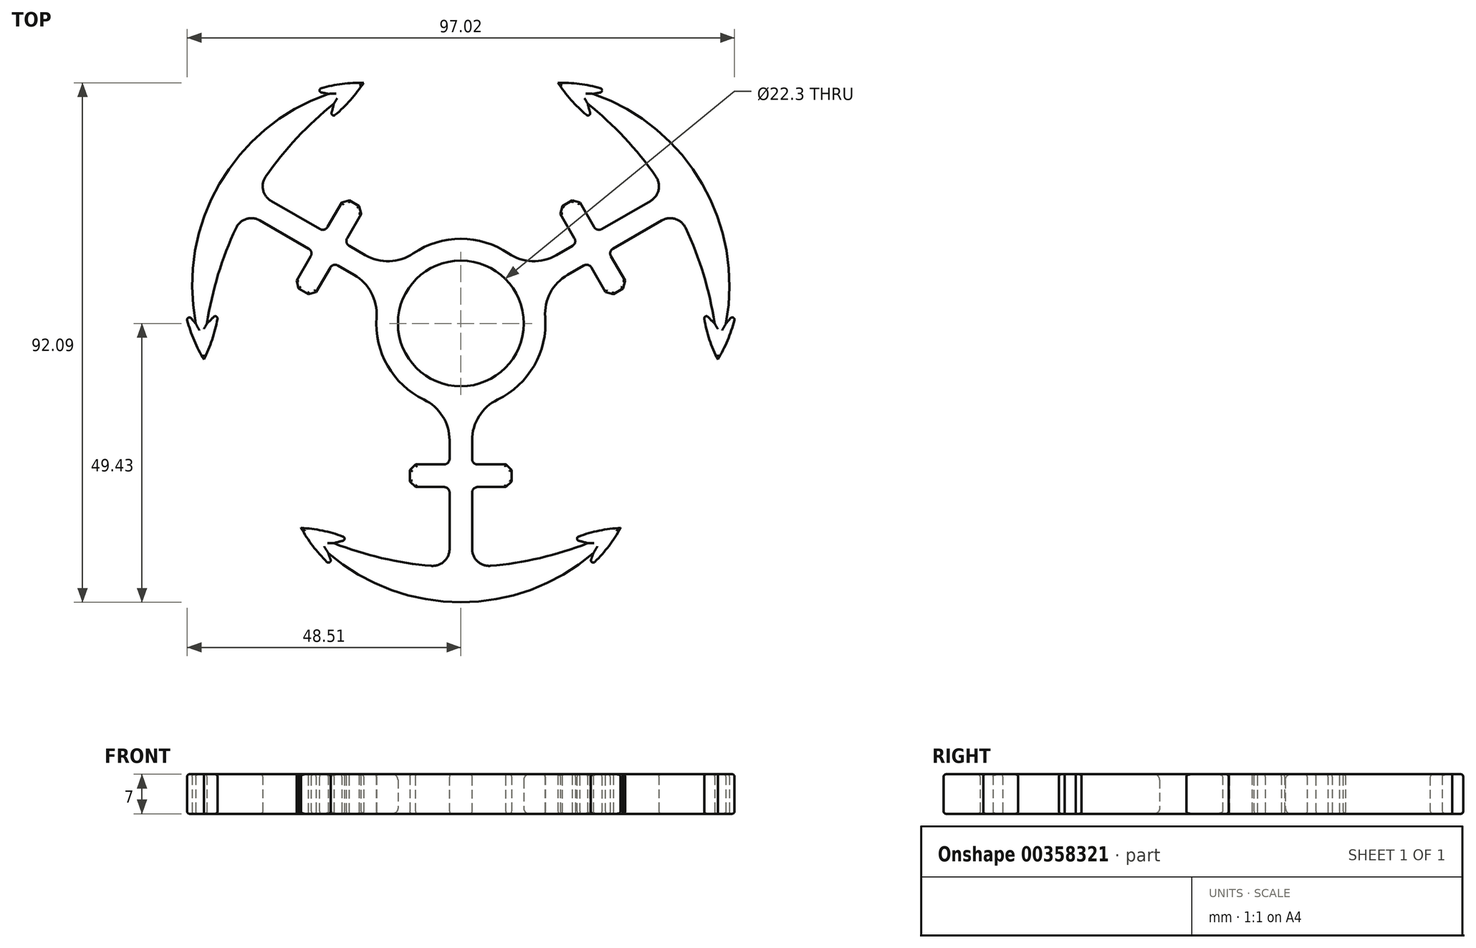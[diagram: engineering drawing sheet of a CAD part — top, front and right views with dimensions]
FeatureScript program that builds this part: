
annotation { "Feature Type Name" : "Feature", "Feature Type Description" : "" }
export const myFeature = defineFeature(function(context is Context, id is Id, definition is map)
    precondition{}
    {
        {
            var Q0;
            Q0=qCreatedBy(makeId("Top.planeOp"),FACE);
            var sketch = newSketch(context, id + "F0", { "sketchPlane" : qUnion([Q0])});
            skCircle(sketch, "E0", {"center": v(0, 0) * mm, "radius": 11.15 * mm});
            skArc(sketch, "E1", {"start": v(-13.87, 5.7) * mm, "mid": v(-13, -7.5) * mm, "end": v(-2, -14.87) * mm});
            skCircle(sketch, "E2", {"center": v(0, 0) * mm, "radius": 45 * mm, "construction": true});
            skLineSegment(sketch, "E3", {"start": v(0, 0) * mm, "end": v(0, -53.16) * mm, "construction": true});
            skLineSegment(sketch, "E4", {"start": v(0, 0) * mm, "end": v(-28.72, -49.74) * mm, "construction": true});
            skLineSegment(sketch, "E5", {"start": v(0, 0) * mm, "end": v(28.85, -49.97) * mm, "construction": true});
            skCircle(sketch, "E6.0", {"center": v(0, 0) * mm, "radius": 47 * mm, "construction": true});
            skArc(sketch, "E7", {"start": v(-22.5, -38.97) * mm, "mid": v(-12.43, -41.94) * mm, "end": v(-2, -43.17) * mm});
            skArc(sketch, "E8", {"start": v(-23.5, -40.7) * mm, "mid": v(0, -49.43) * mm, "end": v(23.5, -40.7) * mm});
            skLineSegment(sketch, "E9", {"start": v(0, 0) * mm, "end": v(-34.06, -43.6) * mm, "construction": true});
            skLineSegment(sketch, "E10", {"start": v(0, 0) * mm, "end": v(33.07, -42.33) * mm, "construction": true});
            skCircle(sketch, "E11.0", {"center": v(0, 0) * mm, "radius": 46 * mm, "construction": true});
            skCircle(sketch, "E12.0", {"center": v(0, 0) * mm, "radius": 43 * mm, "construction": true});
            skCircle(sketch, "E13.0", {"center": v(0, 0) * mm, "radius": 49 * mm, "construction": true});
            skLineSegment(sketch, "E14", {"start": v(0, 0) * mm, "end": v(-25.8, -50.64) * mm, "construction": true});
            skLineSegment(sketch, "E15", {"start": v(0, 0) * mm, "end": v(25.98, -51) * mm, "construction": true});
            skArc(sketch, "E16", {"start": v(-19.52, -38.31) * mm, "mid": v(-23.83, -36.9) * mm, "end": v(-28.32, -36.25) * mm});
            skArc(sketch, "E17", {"start": v(-28.32, -36.25) * mm, "mid": v(-25.63, -40.24) * mm, "end": v(-22.25, -43.66) * mm});
            skArc(sketch, "E18", {"start": v(-23.5, -40.7) * mm, "mid": v(-22.95, -42.21) * mm, "end": v(-22.25, -43.66) * mm});
            skArc(sketch, "E19", {"start": v(-19.52, -38.31) * mm, "mid": v(-21.03, -38.57) * mm, "end": v(-22.5, -38.97) * mm});
            skArc(sketch, "E20", {"start": v(28.32, -36.25) * mm, "mid": v(23.83, -36.9) * mm, "end": v(19.52, -38.31) * mm});
            skArc(sketch, "E21", {"start": v(22.25, -43.66) * mm, "mid": v(25.63, -40.24) * mm, "end": v(28.32, -36.25) * mm});
            skArc(sketch, "E22", {"start": v(22.25, -43.66) * mm, "mid": v(22.95, -42.21) * mm, "end": v(23.5, -40.7) * mm});
            skArc(sketch, "E23", {"start": v(22.5, -38.97) * mm, "mid": v(21.03, -38.57) * mm, "end": v(19.52, -38.31) * mm});
            skArc(sketch, "E24.trimOffspring", {"start": v(2, -43.17) * mm, "mid": v(12.43, -41.94) * mm, "end": v(22.5, -38.97) * mm});
            skLineSegment(sketch, "E25.trimOffspring", {"start": v(-2, -14.87) * mm, "end": v(-2, -43.17) * mm});
            skLineSegment(sketch, "E26.trimOffspring", {"start": v(2, -14.87) * mm, "end": v(2, -43.17) * mm});
            skArc(sketch, "E27.1.0", {"start": v(42.94, 2.25) * mm, "mid": v(43.91, 1.07) * mm, "end": v(45, 0) * mm});
            skArc(sketch, "E27.1.1", {"start": v(45.55, -6.4) * mm, "mid": v(47.66, -2.08) * mm, "end": v(48.93, 2.56) * mm});
            skArc(sketch, "E27.1.2", {"start": v(22.5, 38.97) * mm, "mid": v(22.89, 37.5) * mm, "end": v(23.42, 36.06) * mm});
            skArc(sketch, "E27.1.3", {"start": v(42.94, 2.25) * mm, "mid": v(43.87, -2.2) * mm, "end": v(45.55, -6.4) * mm});
            skArc(sketch, "E27.1.4", {"start": v(17.23, 42.65) * mm, "mid": v(20.04, 39.09) * mm, "end": v(23.42, 36.06) * mm});
            skArc(sketch, "E27.1.5", {"start": v(26.69, 41.1) * mm, "mid": v(22.03, 42.31) * mm, "end": v(17.23, 42.65) * mm});
            skArc(sketch, "E27.1.6", {"start": v(36.38, 23.31) * mm, "mid": v(30.1, 31.73) * mm, "end": v(22.5, 38.97) * mm});
            skArc(sketch, "E27.1.7", {"start": v(47, 0) * mm, "mid": v(42.8, 24.72) * mm, "end": v(23.5, 40.7) * mm});
            skArc(sketch, "E27.1.8", {"start": v(45, 0) * mm, "mid": v(42.53, 10.2) * mm, "end": v(38.38, 19.85) * mm});
            skArc(sketch, "E27.1.9", {"start": v(47, 0) * mm, "mid": v(48.04, 1.23) * mm, "end": v(48.93, 2.56) * mm});
            skArc(sketch, "E27.1.10", {"start": v(26.69, 41.1) * mm, "mid": v(25.08, 40.98) * mm, "end": v(23.5, 40.7) * mm});
            skLineSegment(sketch, "E27.1.11", {"start": v(13.87, 5.7) * mm, "end": v(38.38, 19.85) * mm});
            skLineSegment(sketch, "E27.1.12", {"start": v(11.87, 9.17) * mm, "end": v(36.38, 23.31) * mm});
            skArc(sketch, "E27.2.0", {"start": v(-23.42, 36.06) * mm, "mid": v(-22.89, 37.5) * mm, "end": v(-22.5, 38.97) * mm});
            skArc(sketch, "E27.2.1", {"start": v(-17.23, 42.65) * mm, "mid": v(-22.03, 42.31) * mm, "end": v(-26.69, 41.1) * mm});
            skArc(sketch, "E27.2.2", {"start": v(-45, 0) * mm, "mid": v(-43.91, 1.07) * mm, "end": v(-42.94, 2.25) * mm});
            skArc(sketch, "E27.2.3", {"start": v(-23.42, 36.06) * mm, "mid": v(-20.04, 39.09) * mm, "end": v(-17.23, 42.65) * mm});
            skArc(sketch, "E27.2.4", {"start": v(-45.55, -6.4) * mm, "mid": v(-43.87, -2.2) * mm, "end": v(-42.94, 2.25) * mm});
            skArc(sketch, "E27.2.5", {"start": v(-48.93, 2.56) * mm, "mid": v(-47.66, -2.08) * mm, "end": v(-45.55, -6.4) * mm});
            skArc(sketch, "E27.2.6", {"start": v(-38.38, 19.85) * mm, "mid": v(-42.53, 10.2) * mm, "end": v(-45, 0) * mm});
            skArc(sketch, "E27.2.7", {"start": v(-23.5, 40.7) * mm, "mid": v(-42.8, 24.72) * mm, "end": v(-47, 0) * mm});
            skArc(sketch, "E27.2.8", {"start": v(-22.5, 38.97) * mm, "mid": v(-30.1, 31.73) * mm, "end": v(-36.38, 23.31) * mm});
            skArc(sketch, "E27.2.9", {"start": v(-23.5, 40.7) * mm, "mid": v(-25.08, 40.98) * mm, "end": v(-26.69, 41.1) * mm});
            skArc(sketch, "E27.2.10", {"start": v(-48.93, 2.56) * mm, "mid": v(-48.04, 1.23) * mm, "end": v(-47, 0) * mm});
            skLineSegment(sketch, "E27.2.11", {"start": v(-11.87, 9.17) * mm, "end": v(-36.38, 23.31) * mm});
            skLineSegment(sketch, "E27.2.12", {"start": v(-13.87, 5.7) * mm, "end": v(-38.38, 19.85) * mm});
            skArc(sketch, "E28.trimOffspring", {"start": v(11.87, 9.17) * mm, "mid": v(0, 15) * mm, "end": v(-11.87, 9.17) * mm});
            skArc(sketch, "E29.trimOffspring", {"start": v(2, -14.87) * mm, "mid": v(13, -7.5) * mm, "end": v(13.87, 5.7) * mm});
            skSolve(sketch);
        }
        {
            var Q0;
            Q0 = qSketchRegion(id + "F0", true);
            extrude(context, id + "F1", {"entities" : qUnion([Q0]), "depth" : 7 * mm});
        }
        {
            var Q0;
            Q0=makeQuery(id+"F1.opExtrude","SWEPT_EDGE",EDGE,{"disambiguationData":[OSD([sQuery(id+"F0.wireOp",EDGE,"E26.trimOffspring"),sQuery(id+"F0.wireOp",EDGE,"E29.trimOffspring")])]});
            var Q1;
            Q1=makeQuery(id+"F1.opExtrude","SWEPT_EDGE",EDGE,{"disambiguationData":[OSD([sQuery(id+"F0.wireOp",EDGE,"E27.2.11"),sQuery(id+"F0.wireOp",EDGE,"E28.trimOffspring")])]});
            var Q2;
            Q2=makeQuery(id+"F1.opExtrude","SWEPT_EDGE",EDGE,{"disambiguationData":[OSD([sQuery(id+"F0.wireOp",EDGE,"E27.1.12"),sQuery(id+"F0.wireOp",EDGE,"E28.trimOffspring")])]});
            var Q3;
            Q3=makeQuery(id+"F1.opExtrude","SWEPT_EDGE",EDGE,{"disambiguationData":[OSD([sQuery(id+"F0.wireOp",EDGE,"E27.1.11"),sQuery(id+"F0.wireOp",EDGE,"E29.trimOffspring")])]});
            var Q4;
            Q4=makeQuery(id+"F1.opExtrude","SWEPT_EDGE",EDGE,{"disambiguationData":[OSD([sQuery(id+"F0.wireOp",EDGE,"E1"),sQuery(id+"F0.wireOp",EDGE,"E27.2.12")])]});
            var Q5;
            Q5=makeQuery(id+"F1.opExtrude","SWEPT_EDGE",EDGE,{"disambiguationData":[OSD([sQuery(id+"F0.wireOp",EDGE,"E1"),sQuery(id+"F0.wireOp",EDGE,"E25.trimOffspring")])]});
            fillet(context, id + "F2", {"entities" : qUnion([Q0, Q1, Q2, Q3, Q4, Q5]), "radius" : 8 * mm, "tangentPropagation" : true, "allowEdgeOverflow" : false});
        }
        {
            var Q0;
            Q0=makeQuery(id+"F1.opExtrude","SWEPT_EDGE",EDGE,{"disambiguationData":[OSD([sQuery(id+"F0.wireOp",EDGE,"E27.1.6"),sQuery(id+"F0.wireOp",EDGE,"E27.1.12")])]});
            var Q1;
            Q1=makeQuery(id+"F1.opExtrude","SWEPT_EDGE",EDGE,{"disambiguationData":[OSD([sQuery(id+"F0.wireOp",EDGE,"E7"),sQuery(id+"F0.wireOp",EDGE,"E25.trimOffspring")])]});
            var Q2;
            Q2=makeQuery(id+"F1.opExtrude","SWEPT_EDGE",EDGE,{"disambiguationData":[OSD([sQuery(id+"F0.wireOp",EDGE,"E27.2.8"),sQuery(id+"F0.wireOp",EDGE,"E27.2.11")])]});
            var Q3;
            Q3=makeQuery(id+"F1.opExtrude","SWEPT_EDGE",EDGE,{"disambiguationData":[OSD([sQuery(id+"F0.wireOp",EDGE,"E27.2.6"),sQuery(id+"F0.wireOp",EDGE,"E27.2.12")])]});
            var Q4;
            Q4=makeQuery(id+"F1.opExtrude","SWEPT_EDGE",EDGE,{"disambiguationData":[OSD([sQuery(id+"F0.wireOp",EDGE,"E27.1.8"),sQuery(id+"F0.wireOp",EDGE,"E27.1.11")])]});
            var Q5;
            Q5=makeQuery(id+"F1.opExtrude","SWEPT_EDGE",EDGE,{"disambiguationData":[OSD([sQuery(id+"F0.wireOp",EDGE,"E24.trimOffspring"),sQuery(id+"F0.wireOp",EDGE,"E26.trimOffspring")])]});
            fillet(context, id + "F3", {"entities" : qUnion([Q0, Q1, Q2, Q3, Q4, Q5]), "radius" : 3 * mm, "tangentPropagation" : true, "allowEdgeOverflow" : false});
        }
        {
            var Q0;
            Q0=makeQuery(id+"F1.opExtrude","SWEPT_EDGE",EDGE,{"disambiguationData":[OSD([sQuery(id+"F0.wireOp",EDGE,"E27.2.0"),sQuery(id+"F0.wireOp",EDGE,"E27.2.3")])]});
            var Q1;
            Q1=makeQuery(id+"F1.opExtrude","SWEPT_EDGE",EDGE,{"disambiguationData":[OSD([sQuery(id+"F0.wireOp",EDGE,"E27.2.1"),sQuery(id+"F0.wireOp",EDGE,"E27.2.9")])]});
            var Q2;
            Q2=makeQuery(id+"F1.opExtrude","SWEPT_EDGE",EDGE,{"disambiguationData":[OSD([sQuery(id+"F0.wireOp",EDGE,"E27.2.5"),sQuery(id+"F0.wireOp",EDGE,"E27.2.10")])]});
            var Q3;
            Q3=makeQuery(id+"F1.opExtrude","SWEPT_EDGE",EDGE,{"disambiguationData":[OSD([sQuery(id+"F0.wireOp",EDGE,"E27.2.2"),sQuery(id+"F0.wireOp",EDGE,"E27.2.4")])]});
            var Q4;
            Q4=makeQuery(id+"F1.opExtrude","SWEPT_EDGE",EDGE,{"disambiguationData":[OSD([sQuery(id+"F0.wireOp",EDGE,"E27.1.2"),sQuery(id+"F0.wireOp",EDGE,"E27.1.4")])]});
            var Q5;
            Q5=makeQuery(id+"F1.opExtrude","SWEPT_EDGE",EDGE,{"disambiguationData":[OSD([sQuery(id+"F0.wireOp",EDGE,"E27.1.0"),sQuery(id+"F0.wireOp",EDGE,"E27.1.3")])]});
            var Q6;
            Q6=makeQuery(id+"F1.opExtrude","SWEPT_EDGE",EDGE,{"disambiguationData":[OSD([sQuery(id+"F0.wireOp",EDGE,"E17"),sQuery(id+"F0.wireOp",EDGE,"E18")])]});
            var Q7;
            Q7=makeQuery(id+"F1.opExtrude","SWEPT_EDGE",EDGE,{"disambiguationData":[OSD([sQuery(id+"F0.wireOp",EDGE,"E21"),sQuery(id+"F0.wireOp",EDGE,"E22")])]});
            var Q8;
            Q8=makeQuery(id+"F1.opExtrude","SWEPT_EDGE",EDGE,{"disambiguationData":[OSD([sQuery(id+"F0.wireOp",EDGE,"E20"),sQuery(id+"F0.wireOp",EDGE,"E23")])]});
            var Q9;
            Q9=makeQuery(id+"F1.opExtrude","SWEPT_EDGE",EDGE,{"disambiguationData":[OSD([sQuery(id+"F0.wireOp",EDGE,"E16"),sQuery(id+"F0.wireOp",EDGE,"E19")])]});
            var Q10;
            Q10=makeQuery(id+"F1.opExtrude","SWEPT_EDGE",EDGE,{"disambiguationData":[OSD([sQuery(id+"F0.wireOp",EDGE,"E27.1.5"),sQuery(id+"F0.wireOp",EDGE,"E27.1.10")])]});
            var Q11;
            Q11=makeQuery(id+"F1.opExtrude","SWEPT_EDGE",EDGE,{"disambiguationData":[OSD([sQuery(id+"F0.wireOp",EDGE,"E27.1.1"),sQuery(id+"F0.wireOp",EDGE,"E27.1.9")])]});
            fillet(context, id + "F4", {"entities" : qUnion([Q0, Q1, Q2, Q3, Q4, Q5, Q6, Q7, Q8, Q9, Q10, Q11]), "radius" : .4 * mm, "allowEdgeOverflow" : false});
        }
        {
            var Q0;
            Q0=qCreatedBy(makeId("Top.planeOp"),FACE);
            var sketch = newSketch(context, id + "F5", { "sketchPlane" : qUnion([Q0])});
            skLineSegment(sketch, "E30.bottom", {"start": v(-9, -25) * mm, "end": v(9, -25) * mm});
            skLineSegment(sketch, "E30.top", {"start": v(-9, -29) * mm, "end": v(9, -29) * mm});
            skLineSegment(sketch, "E30.left", {"start": v(-9, -25) * mm, "end": v(-9, -29) * mm});
            skLineSegment(sketch, "E30.right", {"start": v(9, -25) * mm, "end": v(9, -29) * mm});
            skLineSegment(sketch, "E31.1.0", {"start": v(26.15, 4.7) * mm, "end": v(17.15, 20.3) * mm});
            skLineSegment(sketch, "E31.1.1", {"start": v(29.61, 6.7) * mm, "end": v(20.61, 22.3) * mm});
            skLineSegment(sketch, "E31.1.2", {"start": v(26.15, 4.7) * mm, "end": v(29.61, 6.7) * mm});
            skLineSegment(sketch, "E31.1.3", {"start": v(17.15, 20.3) * mm, "end": v(20.61, 22.3) * mm});
            skLineSegment(sketch, "E31.2.0", {"start": v(-17.15, 20.3) * mm, "end": v(-26.15, 4.7) * mm});
            skLineSegment(sketch, "E31.2.1", {"start": v(-20.61, 22.3) * mm, "end": v(-29.61, 6.7) * mm});
            skLineSegment(sketch, "E31.2.2", {"start": v(-17.15, 20.3) * mm, "end": v(-20.61, 22.3) * mm});
            skLineSegment(sketch, "E31.2.3", {"start": v(-26.15, 4.7) * mm, "end": v(-29.61, 6.7) * mm});
            skPoint(sketch, "E31.center", {"position": v(0, 0) * mm});
            skSolve(sketch);
        }
        {
            var Q0;
            Q0 = qSketchRegion(id + "F5", true);
            extrude(context, id + "F6", {"entities" : qUnion([Q0]), "operationType" : NewBodyOperationType.ADD, "depth" : 7 * mm});
        }
        {
            var Q0;
            Q0=makeQuery(id+"F6.opExtrude","SWEPT_EDGE",EDGE,{"disambiguationData":[OSD([sQuery(id+"F5.wireOp",EDGE,"E31.2.0"),sQuery(id+"F5.wireOp",EDGE,"E31.2.3")])]});
            var Q1;
            Q1=makeQuery(id+"F6.opExtrude","SWEPT_EDGE",EDGE,{"disambiguationData":[OSD([sQuery(id+"F5.wireOp",EDGE,"E31.2.1"),sQuery(id+"F5.wireOp",EDGE,"E31.2.3")])]});
            var Q2;
            Q2=makeQuery(id+"F6.opExtrude","SWEPT_EDGE",EDGE,{"disambiguationData":[OSD([sQuery(id+"F5.wireOp",EDGE,"E31.2.0"),sQuery(id+"F5.wireOp",EDGE,"E31.2.2")])]});
            var Q3;
            Q3=makeQuery(id+"F6.opExtrude","SWEPT_EDGE",EDGE,{"disambiguationData":[OSD([sQuery(id+"F5.wireOp",EDGE,"E30.top"),sQuery(id+"F5.wireOp",EDGE,"E30.left")])]});
            var Q4;
            Q4=makeQuery(id+"F6.opExtrude","SWEPT_EDGE",EDGE,{"disambiguationData":[OSD([sQuery(id+"F5.wireOp",EDGE,"E30.top"),sQuery(id+"F5.wireOp",EDGE,"E30.right")])]});
            var Q5;
            Q5=makeQuery(id+"F6.opExtrude","SWEPT_EDGE",EDGE,{"disambiguationData":[OSD([sQuery(id+"F5.wireOp",EDGE,"E31.1.0"),sQuery(id+"F5.wireOp",EDGE,"E31.1.2")])]});
            var Q6;
            Q6=makeQuery(id+"F6.opExtrude","SWEPT_EDGE",EDGE,{"disambiguationData":[OSD([sQuery(id+"F5.wireOp",EDGE,"E31.1.1"),sQuery(id+"F5.wireOp",EDGE,"E31.1.2")])]});
            var Q7;
            Q7=makeQuery(id+"F6.opExtrude","SWEPT_EDGE",EDGE,{"disambiguationData":[OSD([sQuery(id+"F5.wireOp",EDGE,"E31.1.0"),sQuery(id+"F5.wireOp",EDGE,"E31.1.3")])]});
            var Q8;
            Q8=makeQuery(id+"F6.opExtrude","SWEPT_EDGE",EDGE,{"disambiguationData":[OSD([sQuery(id+"F5.wireOp",EDGE,"E30.bottom"),sQuery(id+"F5.wireOp",EDGE,"E30.right")])]});
            var Q9;
            Q9=makeQuery(id+"F6.opExtrude","SWEPT_EDGE",EDGE,{"disambiguationData":[OSD([sQuery(id+"F5.wireOp",EDGE,"E30.bottom"),sQuery(id+"F5.wireOp",EDGE,"E30.left")])]});
            var Q10;
            Q10=makeQuery(id+"F6.opExtrude","SWEPT_EDGE",EDGE,{"disambiguationData":[OSD([sQuery(id+"F5.wireOp",EDGE,"E31.1.1"),sQuery(id+"F5.wireOp",EDGE,"E31.1.3")])]});
            var Q11;
            Q11=makeQuery(id+"F6.opExtrude","SWEPT_EDGE",EDGE,{"disambiguationData":[OSD([sQuery(id+"F5.wireOp",EDGE,"E31.2.1"),sQuery(id+"F5.wireOp",EDGE,"E31.2.2")])]});
            chamfer(context, id + "F7", {"entities" : qUnion([Q0, Q1, Q2, Q3, Q4, Q5, Q6, Q7, Q8, Q9, Q10, Q11]), "width" : 1 * mm, "tangentPropagation" : true});
        }
        {
            var Q0;
            Q0=makeQuery(id+"F1.opExtrude","SWEPT_FACE",FACE,{"disambiguationData":[OSD([sQuery(id+"F0.wireOp",EDGE,"E0")])]});
            fillet(context, id + "F8", {"entities" : qUnion([Q0]), "radius" : 1 * mm, "tangentPropagation" : true, "allowEdgeOverflow" : false});
        }
        {
            var Q0;
            Q0=makeQuery(id+"F6.boolean.opBoolean","INTERSECT",EDGE,{"derivedFrom":[makeQuery(id+"F1.opExtrude","SWEPT_FACE",FACE,{"disambiguationData":[OSD([sQuery(id+"F0.wireOp",EDGE,"E26.trimOffspring")])]}),makeQuery(id+"F6.opExtrude","SWEPT_FACE",FACE,{"disambiguationData":[OSD([sQuery(id+"F5.wireOp",EDGE,"E30.top")])]})]});
            var Q1;
            Q1=makeQuery(id+"F6.boolean.opBoolean","INTERSECT",EDGE,{"derivedFrom":[makeQuery(id+"F1.opExtrude","SWEPT_FACE",FACE,{"disambiguationData":[OSD([sQuery(id+"F0.wireOp",EDGE,"E27.1.11")])]}),makeQuery(id+"F6.opExtrude","SWEPT_FACE",FACE,{"disambiguationData":[OSD([sQuery(id+"F5.wireOp",EDGE,"E31.1.1")])]})]});
            var Q2;
            Q2=makeQuery(id+"F6.boolean.opBoolean","INTERSECT",EDGE,{"derivedFrom":[makeQuery(id+"F1.opExtrude","SWEPT_FACE",FACE,{"disambiguationData":[OSD([sQuery(id+"F0.wireOp",EDGE,"E27.2.12")])]}),makeQuery(id+"F6.opExtrude","SWEPT_FACE",FACE,{"disambiguationData":[OSD([sQuery(id+"F5.wireOp",EDGE,"E31.2.1")])]})]});
            var Q3;
            Q3=makeQuery(id+"F6.boolean.opBoolean","INTERSECT",EDGE,{"derivedFrom":[makeQuery(id+"F1.opExtrude","SWEPT_FACE",FACE,{"disambiguationData":[OSD([sQuery(id+"F0.wireOp",EDGE,"E25.trimOffspring")])]}),makeQuery(id+"F6.opExtrude","SWEPT_FACE",FACE,{"disambiguationData":[OSD([sQuery(id+"F5.wireOp",EDGE,"E30.top")])]})]});
            var Q4;
            Q4=makeQuery(id+"F6.boolean.opBoolean","INTERSECT",EDGE,{"derivedFrom":[makeQuery(id+"F1.opExtrude","SWEPT_FACE",FACE,{"disambiguationData":[OSD([sQuery(id+"F0.wireOp",EDGE,"E27.1.11")])]}),makeQuery(id+"F6.opExtrude","SWEPT_FACE",FACE,{"disambiguationData":[OSD([sQuery(id+"F5.wireOp",EDGE,"E31.1.0")])]})]});
            var Q5;
            Q5=makeQuery(id+"F6.boolean.opBoolean","INTERSECT",EDGE,{"derivedFrom":[makeQuery(id+"F1.opExtrude","SWEPT_FACE",FACE,{"disambiguationData":[OSD([sQuery(id+"F0.wireOp",EDGE,"E27.2.12")])]}),makeQuery(id+"F6.opExtrude","SWEPT_FACE",FACE,{"disambiguationData":[OSD([sQuery(id+"F5.wireOp",EDGE,"E31.2.0")])]})]});
            var Q6;
            Q6=makeQuery(id+"F6.boolean.opBoolean","INTERSECT",EDGE,{"derivedFrom":[makeQuery(id+"F1.opExtrude","SWEPT_FACE",FACE,{"disambiguationData":[OSD([sQuery(id+"F0.wireOp",EDGE,"E25.trimOffspring")])]}),makeQuery(id+"F6.opExtrude","SWEPT_FACE",FACE,{"disambiguationData":[OSD([sQuery(id+"F5.wireOp",EDGE,"E30.bottom")])]})]});
            var Q7;
            Q7=makeQuery(id+"F6.boolean.opBoolean","INTERSECT",EDGE,{"derivedFrom":[makeQuery(id+"F1.opExtrude","SWEPT_FACE",FACE,{"disambiguationData":[OSD([sQuery(id+"F0.wireOp",EDGE,"E27.1.12")])]}),makeQuery(id+"F6.opExtrude","SWEPT_FACE",FACE,{"disambiguationData":[OSD([sQuery(id+"F5.wireOp",EDGE,"E31.1.0")])]})]});
            var Q8;
            Q8=makeQuery(id+"F6.boolean.opBoolean","INTERSECT",EDGE,{"derivedFrom":[makeQuery(id+"F1.opExtrude","SWEPT_FACE",FACE,{"disambiguationData":[OSD([sQuery(id+"F0.wireOp",EDGE,"E27.2.11")])]}),makeQuery(id+"F6.opExtrude","SWEPT_FACE",FACE,{"disambiguationData":[OSD([sQuery(id+"F5.wireOp",EDGE,"E31.2.1")])]})]});
            var Q9;
            Q9=makeQuery(id+"F6.boolean.opBoolean","INTERSECT",EDGE,{"derivedFrom":[makeQuery(id+"F1.opExtrude","SWEPT_FACE",FACE,{"disambiguationData":[OSD([sQuery(id+"F0.wireOp",EDGE,"E27.1.12")])]}),makeQuery(id+"F6.opExtrude","SWEPT_FACE",FACE,{"disambiguationData":[OSD([sQuery(id+"F5.wireOp",EDGE,"E31.1.1")])]})]});
            var Q10;
            Q10=makeQuery(id+"F6.boolean.opBoolean","INTERSECT",EDGE,{"derivedFrom":[makeQuery(id+"F1.opExtrude","SWEPT_FACE",FACE,{"disambiguationData":[OSD([sQuery(id+"F0.wireOp",EDGE,"E26.trimOffspring")])]}),makeQuery(id+"F6.opExtrude","SWEPT_FACE",FACE,{"disambiguationData":[OSD([sQuery(id+"F5.wireOp",EDGE,"E30.bottom")])]})]});
            var Q11;
            Q11=makeQuery(id+"F6.boolean.opBoolean","INTERSECT",EDGE,{"derivedFrom":[makeQuery(id+"F1.opExtrude","SWEPT_FACE",FACE,{"disambiguationData":[OSD([sQuery(id+"F0.wireOp",EDGE,"E27.2.11")])]}),makeQuery(id+"F6.opExtrude","SWEPT_FACE",FACE,{"disambiguationData":[OSD([sQuery(id+"F5.wireOp",EDGE,"E31.2.0")])]})]});
            fillet(context, id + "F9", {"entities" : qUnion([Q0, Q1, Q2, Q3, Q4, Q5, Q6, Q7, Q8, Q9, Q10, Q11]), "radius" : 1 * mm, "tangentPropagation" : true, "allowEdgeOverflow" : false});
        }
        {
            var Q0;
            Q0=makeQuery(id+"F6.boolean.opBoolean","MERGE",FACE,{"derivedFrom":[makeQuery(id+"F1.opExtrude","CAP_FACE",FACE,{"disambiguationData":[OSD([sQuery(id+"F0.wireOp",EDGE,"E0"),sQuery(id+"F0.wireOp",EDGE,"E1"),sQuery(id+"F0.wireOp",EDGE,"E7"),sQuery(id+"F0.wireOp",EDGE,"E8"),sQuery(id+"F0.wireOp",EDGE,"E16"),sQuery(id+"F0.wireOp",EDGE,"E17"),sQuery(id+"F0.wireOp",EDGE,"E18"),sQuery(id+"F0.wireOp",EDGE,"E19"),sQuery(id+"F0.wireOp",EDGE,"E20"),sQuery(id+"F0.wireOp",EDGE,"E21"),sQuery(id+"F0.wireOp",EDGE,"E22"),sQuery(id+"F0.wireOp",EDGE,"E23"),sQuery(id+"F0.wireOp",EDGE,"E24.trimOffspring"),sQuery(id+"F0.wireOp",EDGE,"E25.trimOffspring"),sQuery(id+"F0.wireOp",EDGE,"E26.trimOffspring"),sQuery(id+"F0.wireOp",EDGE,"E27.1.0"),sQuery(id+"F0.wireOp",EDGE,"E27.1.1"),sQuery(id+"F0.wireOp",EDGE,"E27.1.2"),sQuery(id+"F0.wireOp",EDGE,"E27.1.3"),sQuery(id+"F0.wireOp",EDGE,"E27.1.4"),sQuery(id+"F0.wireOp",EDGE,"E27.1.5"),sQuery(id+"F0.wireOp",EDGE,"E27.1.6"),sQuery(id+"F0.wireOp",EDGE,"E27.1.7"),sQuery(id+"F0.wireOp",EDGE,"E27.1.8"),sQuery(id+"F0.wireOp",EDGE,"E27.1.9"),sQuery(id+"F0.wireOp",EDGE,"E27.1.10"),sQuery(id+"F0.wireOp",EDGE,"E27.1.11"),sQuery(id+"F0.wireOp",EDGE,"E27.1.12"),sQuery(id+"F0.wireOp",EDGE,"E27.2.0"),sQuery(id+"F0.wireOp",EDGE,"E27.2.1"),sQuery(id+"F0.wireOp",EDGE,"E27.2.2"),sQuery(id+"F0.wireOp",EDGE,"E27.2.3"),sQuery(id+"F0.wireOp",EDGE,"E27.2.4"),sQuery(id+"F0.wireOp",EDGE,"E27.2.5"),sQuery(id+"F0.wireOp",EDGE,"E27.2.6"),sQuery(id+"F0.wireOp",EDGE,"E27.2.7"),sQuery(id+"F0.wireOp",EDGE,"E27.2.8"),sQuery(id+"F0.wireOp",EDGE,"E27.2.9"),sQuery(id+"F0.wireOp",EDGE,"E27.2.10"),sQuery(id+"F0.wireOp",EDGE,"E27.2.11"),sQuery(id+"F0.wireOp",EDGE,"E27.2.12"),sQuery(id+"F0.wireOp",EDGE,"E28.trimOffspring"),sQuery(id+"F0.wireOp",EDGE,"E29.trimOffspring")])],"isStart":false}),makeQuery(id+"F6.opExtrude","CAP_FACE",FACE,{"disambiguationData":[OSD([sQuery(id+"F5.wireOp",EDGE,"E30.bottom"),sQuery(id+"F5.wireOp",EDGE,"E30.top"),sQuery(id+"F5.wireOp",EDGE,"E30.left"),sQuery(id+"F5.wireOp",EDGE,"E30.right")])],"isStart":false}),makeQuery(id+"F6.opExtrude","CAP_FACE",FACE,{"disambiguationData":[OSD([sQuery(id+"F5.wireOp",EDGE,"E31.1.0"),sQuery(id+"F5.wireOp",EDGE,"E31.1.1"),sQuery(id+"F5.wireOp",EDGE,"E31.1.2"),sQuery(id+"F5.wireOp",EDGE,"E31.1.3")])],"isStart":false}),makeQuery(id+"F6.opExtrude","CAP_FACE",FACE,{"disambiguationData":[OSD([sQuery(id+"F5.wireOp",EDGE,"E31.2.0"),sQuery(id+"F5.wireOp",EDGE,"E31.2.1"),sQuery(id+"F5.wireOp",EDGE,"E31.2.2"),sQuery(id+"F5.wireOp",EDGE,"E31.2.3")])],"isStart":false})]});
            var Q1;
            Q1=makeQuery(id+"F6.boolean.opBoolean","MERGE",FACE,{"derivedFrom":[makeQuery(id+"F1.opExtrude","CAP_FACE",FACE,{"disambiguationData":[OSD([sQuery(id+"F0.wireOp",EDGE,"E0"),sQuery(id+"F0.wireOp",EDGE,"E1"),sQuery(id+"F0.wireOp",EDGE,"E7"),sQuery(id+"F0.wireOp",EDGE,"E8"),sQuery(id+"F0.wireOp",EDGE,"E16"),sQuery(id+"F0.wireOp",EDGE,"E17"),sQuery(id+"F0.wireOp",EDGE,"E18"),sQuery(id+"F0.wireOp",EDGE,"E19"),sQuery(id+"F0.wireOp",EDGE,"E20"),sQuery(id+"F0.wireOp",EDGE,"E21"),sQuery(id+"F0.wireOp",EDGE,"E22"),sQuery(id+"F0.wireOp",EDGE,"E23"),sQuery(id+"F0.wireOp",EDGE,"E24.trimOffspring"),sQuery(id+"F0.wireOp",EDGE,"E25.trimOffspring"),sQuery(id+"F0.wireOp",EDGE,"E26.trimOffspring"),sQuery(id+"F0.wireOp",EDGE,"E27.1.0"),sQuery(id+"F0.wireOp",EDGE,"E27.1.1"),sQuery(id+"F0.wireOp",EDGE,"E27.1.2"),sQuery(id+"F0.wireOp",EDGE,"E27.1.3"),sQuery(id+"F0.wireOp",EDGE,"E27.1.4"),sQuery(id+"F0.wireOp",EDGE,"E27.1.5"),sQuery(id+"F0.wireOp",EDGE,"E27.1.6"),sQuery(id+"F0.wireOp",EDGE,"E27.1.7"),sQuery(id+"F0.wireOp",EDGE,"E27.1.8"),sQuery(id+"F0.wireOp",EDGE,"E27.1.9"),sQuery(id+"F0.wireOp",EDGE,"E27.1.10"),sQuery(id+"F0.wireOp",EDGE,"E27.1.11"),sQuery(id+"F0.wireOp",EDGE,"E27.1.12"),sQuery(id+"F0.wireOp",EDGE,"E27.2.0"),sQuery(id+"F0.wireOp",EDGE,"E27.2.1"),sQuery(id+"F0.wireOp",EDGE,"E27.2.2"),sQuery(id+"F0.wireOp",EDGE,"E27.2.3"),sQuery(id+"F0.wireOp",EDGE,"E27.2.4"),sQuery(id+"F0.wireOp",EDGE,"E27.2.5"),sQuery(id+"F0.wireOp",EDGE,"E27.2.6"),sQuery(id+"F0.wireOp",EDGE,"E27.2.7"),sQuery(id+"F0.wireOp",EDGE,"E27.2.8"),sQuery(id+"F0.wireOp",EDGE,"E27.2.9"),sQuery(id+"F0.wireOp",EDGE,"E27.2.10"),sQuery(id+"F0.wireOp",EDGE,"E27.2.11"),sQuery(id+"F0.wireOp",EDGE,"E27.2.12"),sQuery(id+"F0.wireOp",EDGE,"E28.trimOffspring"),sQuery(id+"F0.wireOp",EDGE,"E29.trimOffspring")])],"isStart":true}),makeQuery(id+"F6.opExtrude","CAP_FACE",FACE,{"disambiguationData":[OSD([sQuery(id+"F5.wireOp",EDGE,"E30.bottom"),sQuery(id+"F5.wireOp",EDGE,"E30.top"),sQuery(id+"F5.wireOp",EDGE,"E30.left"),sQuery(id+"F5.wireOp",EDGE,"E30.right")])],"isStart":true}),makeQuery(id+"F6.opExtrude","CAP_FACE",FACE,{"disambiguationData":[OSD([sQuery(id+"F5.wireOp",EDGE,"E31.1.0"),sQuery(id+"F5.wireOp",EDGE,"E31.1.1"),sQuery(id+"F5.wireOp",EDGE,"E31.1.2"),sQuery(id+"F5.wireOp",EDGE,"E31.1.3")])],"isStart":true}),makeQuery(id+"F6.opExtrude","CAP_FACE",FACE,{"disambiguationData":[OSD([sQuery(id+"F5.wireOp",EDGE,"E31.2.0"),sQuery(id+"F5.wireOp",EDGE,"E31.2.1"),sQuery(id+"F5.wireOp",EDGE,"E31.2.2"),sQuery(id+"F5.wireOp",EDGE,"E31.2.3")])],"isStart":true})]});
            fillet(context, id + "F10", {"entities" : qUnion([Q0, Q1]), "radius" : .4 * mm, "tangentPropagation" : true, "allowEdgeOverflow" : false});
        }
    });
